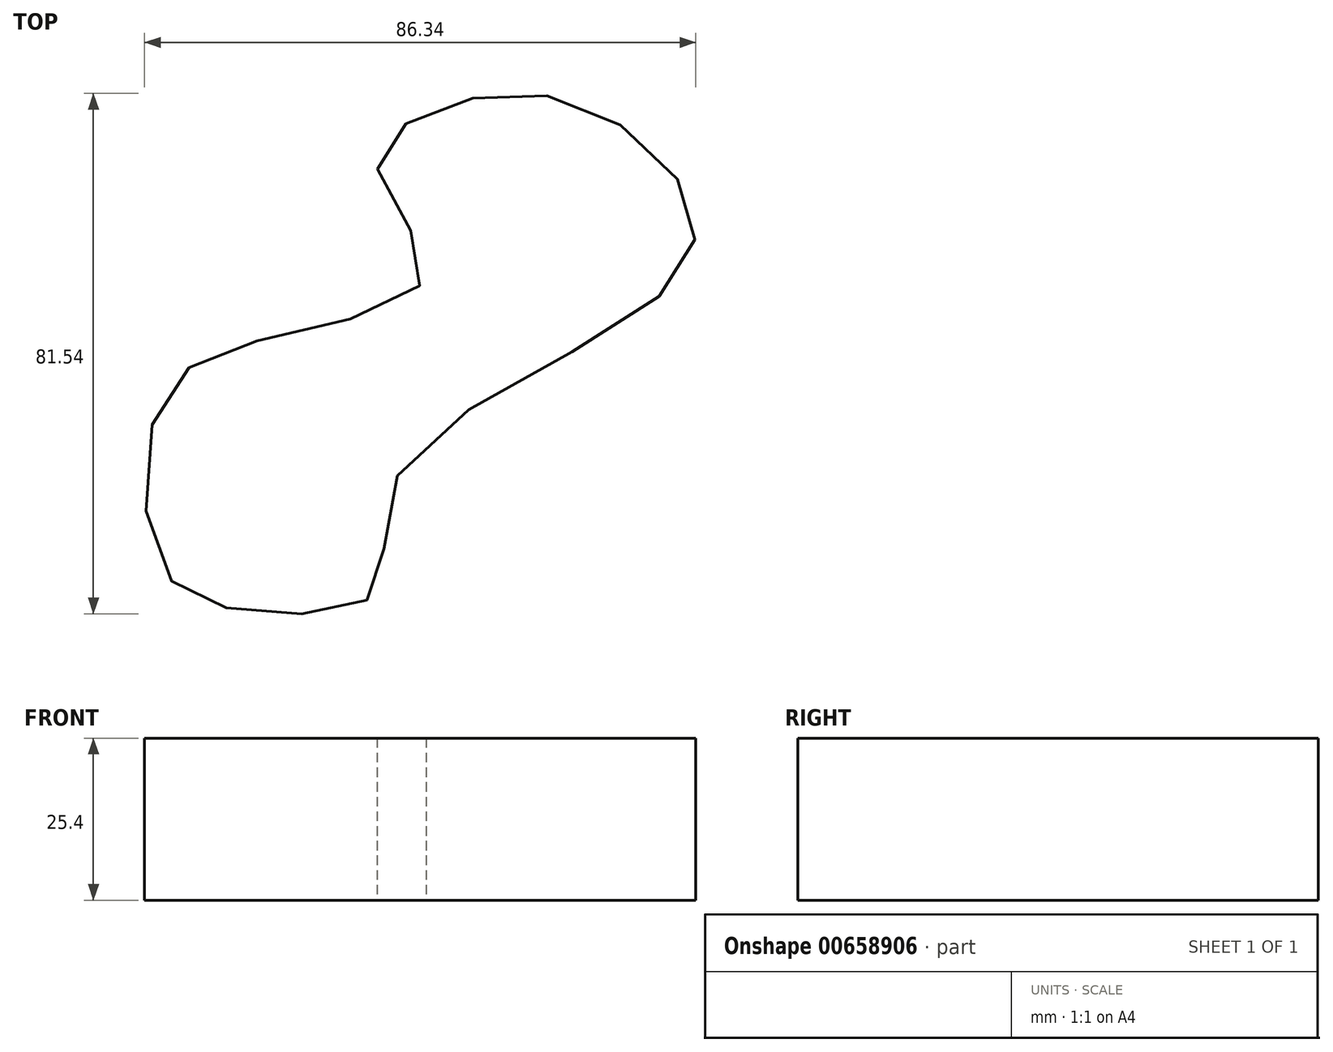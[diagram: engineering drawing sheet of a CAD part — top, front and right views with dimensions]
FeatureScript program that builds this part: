
annotation { "Feature Type Name" : "Feature", "Feature Type Description" : "" }
export const myFeature = defineFeature(function(context is Context, id is Id, definition is map)
    precondition{}
    {
        {
            var Q0;
            Q0=qCreatedBy(makeId("Top.planeOp"),FACE);
            var sketch = newSketch(context, id + "F0", { "sketchPlane" : qUnion([Q0])});
            skFitSpline(sketch, "E0", {"points": [v(0, 0) * mm, v(39.27, 26.7) * mm, v(46.23, 41.88) * mm, v(29.14, 58.02) * mm, v(6.75, 57.71) * mm, v(-3.13, 48.2) * mm, v(4.46, 31.76) * mm, v(-19.9, 21.62) * mm, v(-37.07, 11.6) * mm, v(-36.57, -14.9) * mm, v(-21.52, -21.32) * mm, v(-3.44, -18.22) * mm, v(0, 0) * mm]});
            skSolve(sketch);
        }
        {
            var Q0;
            Q0 = qSketchRegion(id + "F0", true);
            extrude(context, id + "F1", {"entities" : qUnion([Q0]), "depth" : 25.4 * mm, "offsetDistance" : 25.4 * mm});
        }
    });
